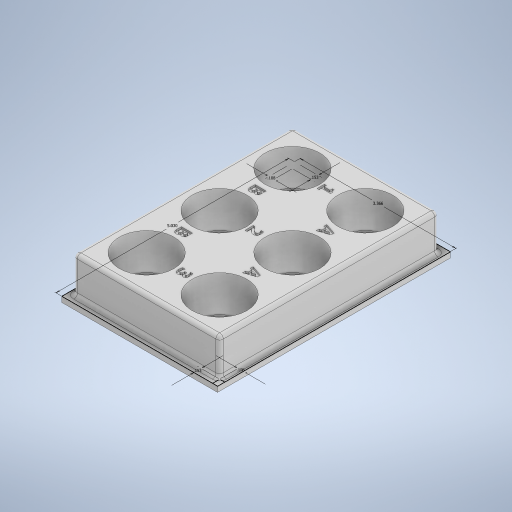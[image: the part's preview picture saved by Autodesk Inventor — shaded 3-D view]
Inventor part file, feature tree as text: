
AUTODESK INVENTOR PART (.ipt)
format: ipt  version: 2024.1 (Build 281209000, 209)  size: 758,272 bytes
history: native  units: in
note: dims shown in document units (in); Inventor stores cm internally (conversion verified against a paired STEP export)
features: extrude x5, fillet x3, sketch x1
ambient origin geometry x8: Origin, YZ Plane, XZ Plane, XY Plane, X Axis, Y Axis, Z Axis, Center Point
bodies: Solid1 (feature_tree)
feature tree (9):
  extrude  "Extrusion1"  Depth=5.0295in
  extrude  "Extrusion2"  Depth=0.1083in
  extrude  "Extrusion3"  Depth=0.1526in
  extrude  "Extrusion4"  Depth=0.1083in
  fillet  "Fillet1"  Radius=0.1526in
  fillet  "Fillet2"  Radius=0.7874in
  fillet  "Fillet3"  Radius=0.1181in
  extrude  "Extrusion5"  Depth=0.7874in
  sketch  "Sketch4"  dims[d0=3.3661in d1=5.0295in d2=0.1083in d3=0.1526in d4=0.1083in d5=0.1526in d6=0.7874in d7=0.0in d8=0.1181in d9=0.0in d10=0.7874in d11=0.7874in d12=1.1811in d13=0.7874in d15=1.5748in d16=1.1811in d18=1.5748in d21=0.7874in d22=0.0in d23=1.2992in d24=0.7874in d26=1.5748in d27=1.1811in d29=1.5748in d32=0.1181in d33=0.1181in d34=0.1181in d35=0.1181in d36=0.7087in d37=0.0in d38=0.125in d39=0.125in d40=0.0787in d41=0.0394in d42=0.0in]
